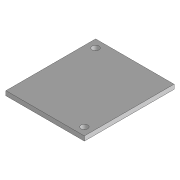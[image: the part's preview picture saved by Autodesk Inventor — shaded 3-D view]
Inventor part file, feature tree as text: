
AUTODESK INVENTOR PART (.ipt)
format: ipt  version: 2022.5 (Build 265521000, 521)  size: 86,528 bytes
history: native  units: mm
features: extrude x2, sketch x1, projected_geometry x1
ambient origin geometry x8: Origin, YZ Plane, XZ Plane, XY Plane, X Axis, Y Axis, Z Axis, Center Point
bodies: Solid1 (feature_tree)
feature tree (4):
  extrude  "Extrusion1"  Depth=40.0mm
  extrude  "Extrusion2"  Depth=35.0mm
  sketch  "Sketch2"  dims[d2=2.0mm d3=0.0mm d7=40.0mm d8=35.0mm d9=3.0mm d10=3.5mm d11=0.0mm d12=0.0mm]
  projected_geometry  "Projected Loop1"
